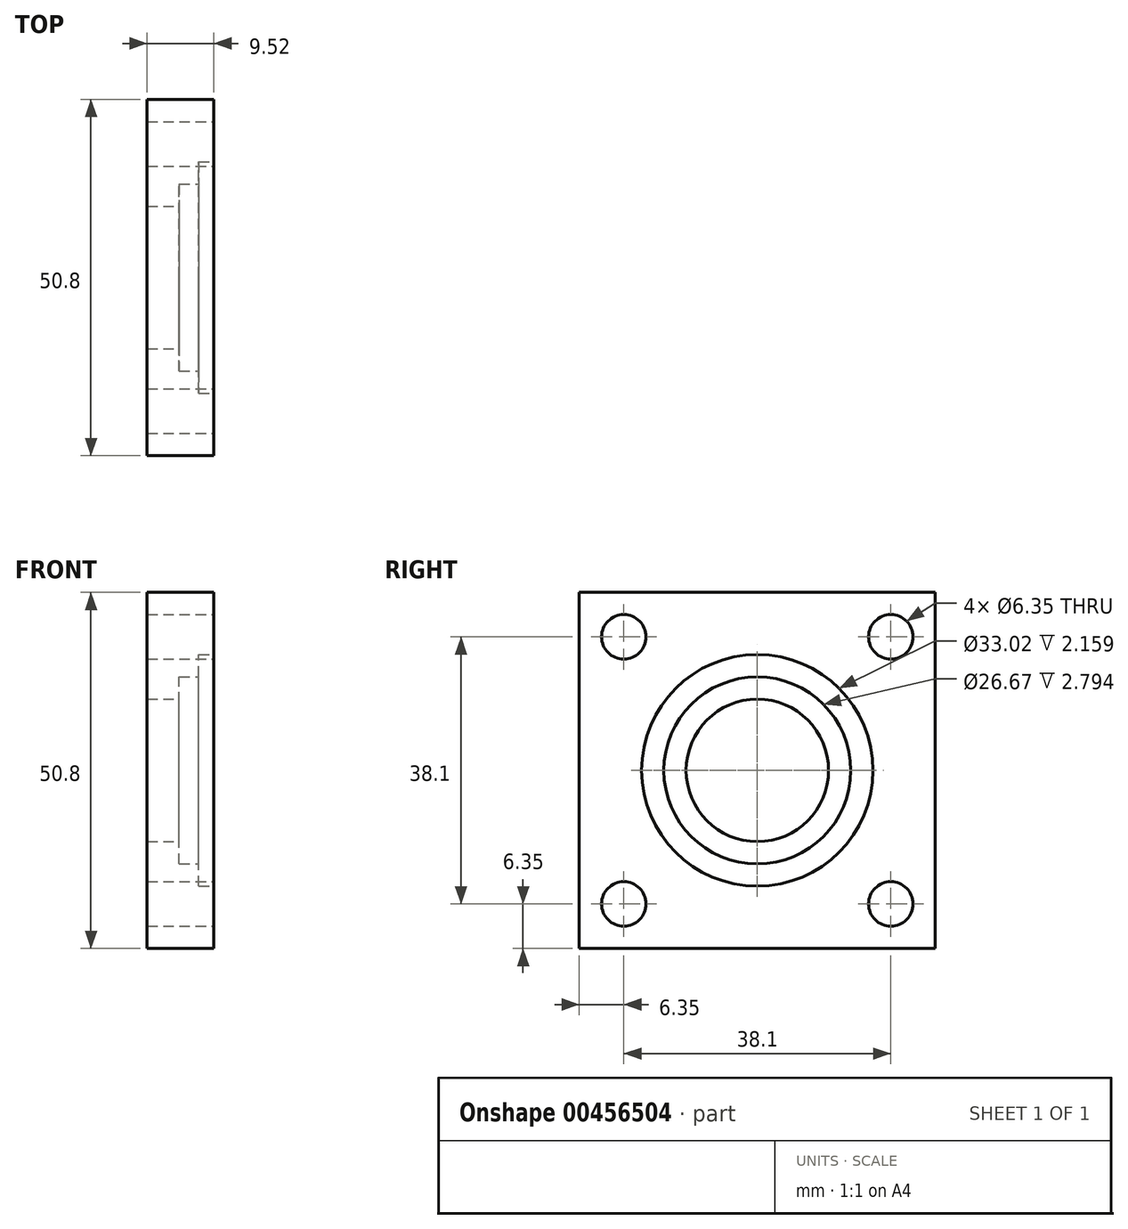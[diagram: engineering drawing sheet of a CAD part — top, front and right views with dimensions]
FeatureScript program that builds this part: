
annotation { "Feature Type Name" : "Feature", "Feature Type Description" : "" }
export const myFeature = defineFeature(function(context is Context, id is Id, definition is map)
    precondition{}
    {
        {
            var Q0;
            Q0=qCreatedBy(makeId("Right.planeOp"),FACE);
            var sketch = newSketch(context, id + "F0", { "sketchPlane" : qUnion([Q0])});
            skLineSegment(sketch, "E0.bottom", {"start": v(25.4, 25.4) * mm, "end": v(-25.4, 25.4) * mm});
            skLineSegment(sketch, "E0.top", {"start": v(25.4, -25.4) * mm, "end": v(-25.4, -25.4) * mm});
            skLineSegment(sketch, "E0.left", {"start": v(25.4, 25.4) * mm, "end": v(25.4, -25.4) * mm});
            skLineSegment(sketch, "E0.right", {"start": v(-25.4, 25.4) * mm, "end": v(-25.4, -25.4) * mm});
            skPoint(sketch, "E0.middle", {"position": v(0, 0) * mm});
            skSolve(sketch);
        }
        {
            var Q0;
            Q0=makeQuery(id+"F0.imprint","IMPRINT",FACE,{"disambiguationData":[TD([[makeQuery(id+"F0.imprint","IMPRINT",EDGE,{"derivedFrom":sQuery(id+"F0.wireOp",EDGE,"E0.bottom")}),1.0]])]});
            extrude(context, id + "F1", {"entities" : qUnion([Q0]), "endBound" : BoundingType.SYMMETRIC, "depth" : 9.52 * mm});
        }
        {
            var Q0;
            Q0=makeQuery(id+"F1.opExtrude","CAP_FACE",FACE,{"disambiguationData":[OSD([sQuery(id+"F0.wireOp",EDGE,"E0.bottom"),sQuery(id+"F0.wireOp",EDGE,"E0.top"),sQuery(id+"F0.wireOp",EDGE,"E0.left"),sQuery(id+"F0.wireOp",EDGE,"E0.right")])],"isStart":false});
            var sketch = newSketch(context, id + "F2", { "sketchPlane" : qUnion([Q0])});
            skCircle(sketch, "E1", {"center": v(0, 0) * mm, "radius": 10.16 * mm});
            skSolve(sketch);
        }
        {
            var Q0;
            Q0=makeQuery(id+"F2.imprint","IMPRINT",FACE,{"disambiguationData":[TD([[makeQuery(id+"F2.imprint","IMPRINT",EDGE,{"derivedFrom":sQuery(id+"F2.wireOp",EDGE,"E1")}),1.0]])]});
            extrude(context, id + "F3", {"entities" : qUnion([Q0]), "operationType" : NewBodyOperationType.REMOVE, "endBound" : BoundingType.UP_TO_NEXT, "oppositeDirection" : true, "depth" : 25.4 * mm});
        }
        {
            var Q0;
            Q0=makeQuery(id+"F1.opExtrude","CAP_FACE",FACE,{"disambiguationData":[OSD([sQuery(id+"F0.wireOp",EDGE,"E0.bottom"),sQuery(id+"F0.wireOp",EDGE,"E0.top"),sQuery(id+"F0.wireOp",EDGE,"E0.left"),sQuery(id+"F0.wireOp",EDGE,"E0.right")])],"isStart":false});
            var sketch = newSketch(context, id + "F4", { "sketchPlane" : qUnion([Q0])});
            skCircle(sketch, "E2", {"center": v(0, 0) * mm, "radius": 16.51 * mm});
            skSolve(sketch);
        }
        {
            var Q0;
            Q0 = qSketchRegion(id + "F4", true);
            extrude(context, id + "F5", {"entities" : qUnion([Q0]), "operationType" : NewBodyOperationType.REMOVE, "oppositeDirection" : true, "depth" : 2.16 * mm});
        }
        {
            var Q0;
            Q0=makeQuery(id+"F1.opExtrude","CAP_FACE",FACE,{"disambiguationData":[OSD([sQuery(id+"F0.wireOp",EDGE,"E0.bottom"),sQuery(id+"F0.wireOp",EDGE,"E0.top"),sQuery(id+"F0.wireOp",EDGE,"E0.left"),sQuery(id+"F0.wireOp",EDGE,"E0.right")])],"isStart":false});
            var sketch = newSketch(context, id + "F6", { "sketchPlane" : qUnion([Q0])});
            skCircle(sketch, "E3", {"center": v(-19.05, 19.05) * mm, "radius": 3.18 * mm});
            skCircle(sketch, "E4.MirrorC", {"center": v(19.05, 19.05) * mm, "radius": 3.18 * mm});
            skCircle(sketch, "E5.MirrorC", {"center": v(-19.05, -19.05) * mm, "radius": 3.18 * mm});
            skCircle(sketch, "E6.MirrorC", {"center": v(19.05, -19.05) * mm, "radius": 3.18 * mm});
            skSolve(sketch);
        }
        {
            var Q0;
            Q0 = qSketchRegion(id + "F6", true);
            extrude(context, id + "F7", {"entities" : qUnion([Q0]), "operationType" : NewBodyOperationType.REMOVE, "endBound" : BoundingType.UP_TO_NEXT, "oppositeDirection" : true, "depth" : 25.4 * mm});
        }
        {
            var Q0;
            Q0=makeQuery(id+"F1.opExtrude","CAP_FACE",FACE,{"disambiguationData":[OSD([sQuery(id+"F0.wireOp",EDGE,"E0.bottom"),sQuery(id+"F0.wireOp",EDGE,"E0.top"),sQuery(id+"F0.wireOp",EDGE,"E0.left"),sQuery(id+"F0.wireOp",EDGE,"E0.right")])],"isStart":false});
            var sketch = newSketch(context, id + "F8", { "sketchPlane" : qUnion([Q0])});
            skCircle(sketch, "E7", {"center": v(0, 0) * mm, "radius": 13.34 * mm});
            skSolve(sketch);
        }
        {
            var Q0;
            Q0 = qSketchRegion(id + "F8", true);
            extrude(context, id + "F9", {"entities" : qUnion([Q0]), "operationType" : NewBodyOperationType.REMOVE, "oppositeDirection" : true, "depth" : 4.95 * mm});
        }
    });
